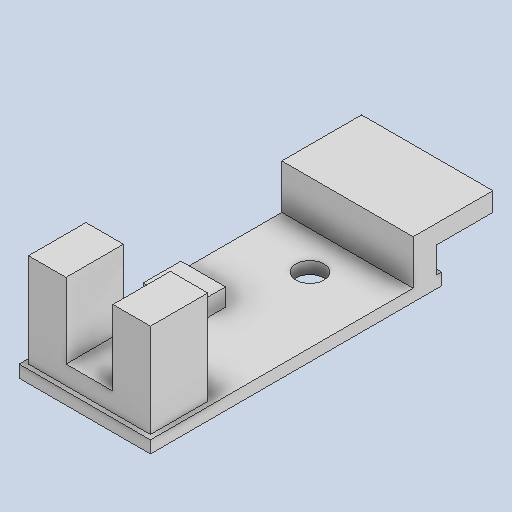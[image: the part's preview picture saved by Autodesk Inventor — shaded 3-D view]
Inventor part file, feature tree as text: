
AUTODESK INVENTOR PART (.ipt)
format: ipt  version: 2022 (Build 260153070, 153G)  size: 136,192 bytes
history: native  units: in
note: dims shown in document units (in); Inventor stores cm internally (conversion verified against a paired STEP export)
features: other x3, sketch x3
ambient origin geometry x8: Origin, YZ Plane, XZ Plane, XY Plane, X Axis, Y Axis, Z Axis, Center Point
bodies: Solid1 (feature_tree)
feature tree (6):
  other  "LM393 encoder.ipt"
  other  "Solid1::LM393 encoder.ipt"
  other  "TaggingFeature1"
  sketch  "Sketch1"  dims[d0=0.3937in]
  sketch  "Sketch2"
  sketch  "Sketch3"
